# Revit family: P710088-031
name_source: partatom
category: Lighting Fixtures
revit_build: Autodesk Revit 2014 (Build: 20130308_1515(x64)
units: mm (PartAtom-declared; Revit-internal decimal feet)

## types (1)
- P710088-031
    Apparent Load = 17 VA
    Assembly Code = D5020200
    Color Filter = 16777215
    Connector Description = Lighting Connector
    Default Elevation = 48"
    Depth = 4"
    Description = Ease yourself into a state of complete bliss and relaxation under the luxurious glow of this wall sconce. A stunning, cylinder-shaped etched opal glass diffuser held in place by a thin metal bar recalls visions of elegant candlesticks. The diffuser sits on top of a pedestal-like light base attached to a beautiful black backplate.
    Dimming Lamp Color Temperature Shift = <None>
    Fixture distribution = Direct
    Glass = Hubbell - Glass
    Gold = Hubbell - Gold
    Height = 18"
    Housing Material = Paint - Hubbell - Textured Camera Black
    Lamp = LED or Incandescent
    Load Classification = Lighting
    Manufacturer = Progress Lighting
    Model = P710088-031
    Photometric Web File = generic
    Power Factor = 1
    Product Documentation Link = https://hubbellcdn.com
    Product Link = https://www.hubbell.com
    Specifications = A stunning, cylinder-shaped etched opal glass diffuser held in place by a thin metal bar recalls visions of elegant candlesticks.
The diffuser sits on top of a pedestal-like light base attached to a beautiful black backplate.
Ease yourself into a state of complete bliss and relaxation under the luxurious glow of this wall sconce.
Ideal for any bedroom, living room, sitting room, hallway, foyer, or bathroom.
Perfect for modern, contemporary, and luxury settings.
Measures 5-inch width by 18-inch height.
Uses one medium base bulb that is sold separately (60w max - LED or incandescent).
Able to be fully dimmable with dimmable bulbs.
Includes installation instructions and mounting hardware.
Progress Lighting products are designed for exceptional quality, reliability, and functionality.
    Tilt Angle = 60.00°
    URL = https://www.hubbell.com
    Voltage = 120 V
    Warranty = 1 year Warranty
    Wattage Comments = 60w
    Watts = 17 W
    White = Paint - Hubbell - Matte White
    Width = 5"

## geometry (parser evidence)
native form markers: Sweep x3
no freeform markers — native parametric forms only
